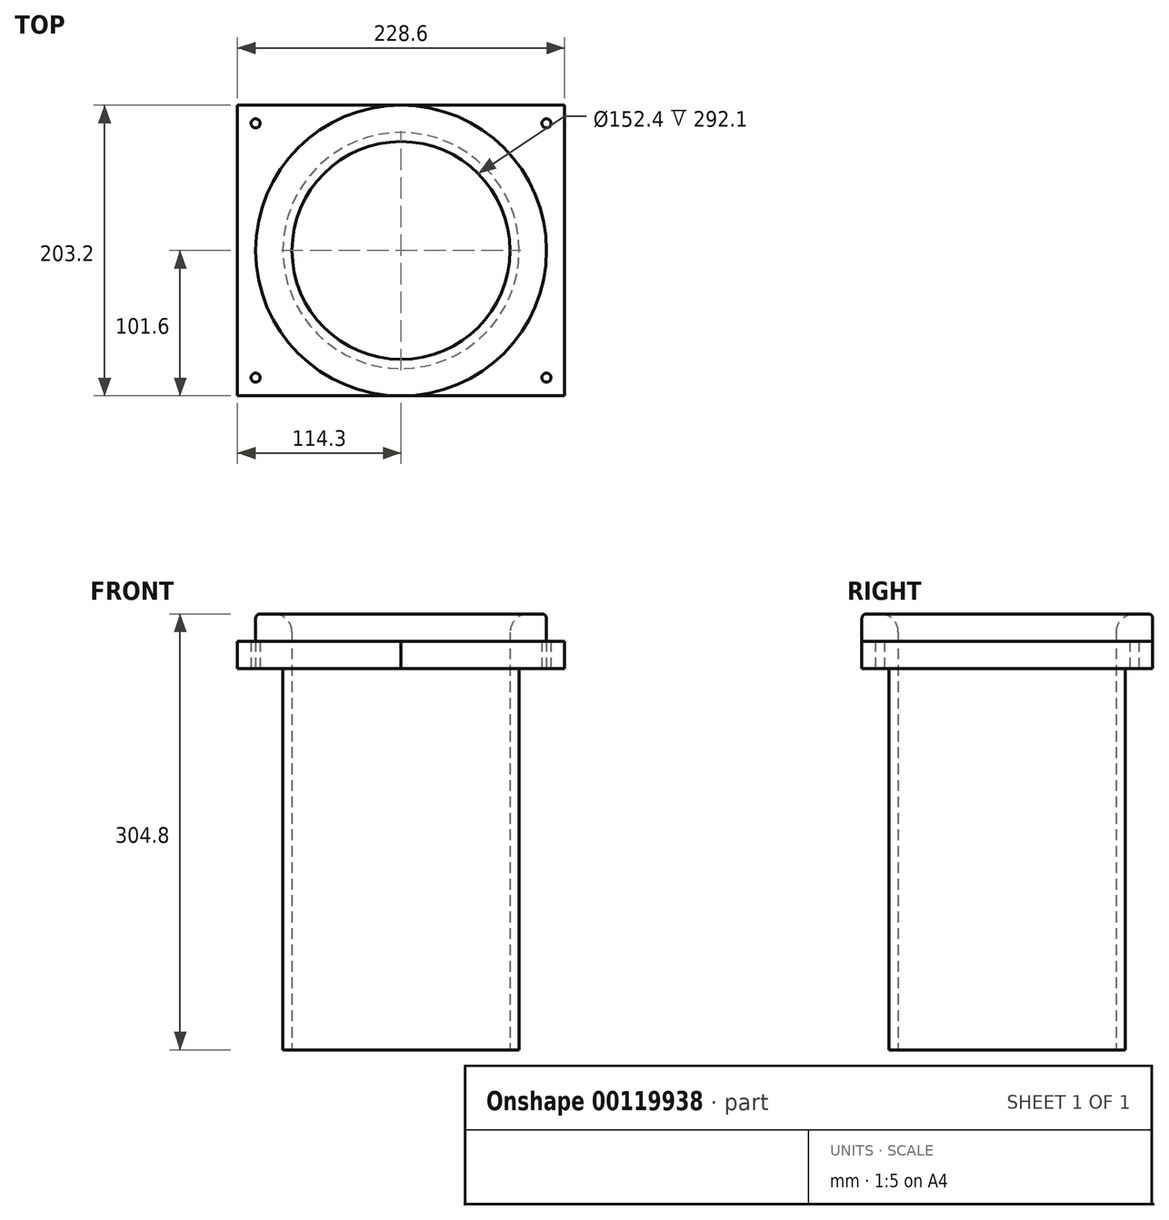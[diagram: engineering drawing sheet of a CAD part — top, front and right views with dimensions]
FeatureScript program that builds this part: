
annotation { "Feature Type Name" : "Feature", "Feature Type Description" : "" }
export const myFeature = defineFeature(function(context is Context, id is Id, definition is map)
    precondition{}
    {
        {
            var Q0;
            Q0=qCreatedBy(makeId("Top.planeOp"),FACE);
            var sketch = newSketch(context, id + "F0", { "sketchPlane" : qUnion([Q0])});
            skLineSegment(sketch, "E0.bottom", {"start": v(0, 0) * mm, "end": v(228.6, 0) * mm});
            skLineSegment(sketch, "E0.top", {"start": v(0, 203.2) * mm, "end": v(228.6, 203.2) * mm});
            skLineSegment(sketch, "E0.left", {"start": v(0, 0) * mm, "end": v(0, 203.2) * mm});
            skLineSegment(sketch, "E0.right", {"start": v(228.6, 0) * mm, "end": v(228.6, 203.2) * mm});
            skCircle(sketch, "E1", {"center": v(114.3, 101.6) * mm, "radius": 76.2 * mm});
            skCircle(sketch, "E2", {"center": v(114.3, 101.6) * mm, "radius": 82.55 * mm});
            skCircle(sketch, "E3", {"center": v(114.3, 101.6) * mm, "radius": 101.6 * mm});
            skCircle(sketch, "E4", {"center": v(12.7, 190.5) * mm, "radius": 3.18 * mm});
            skCircle(sketch, "E5", {"center": v(12.7, 12.7) * mm, "radius": 3.18 * mm});
            skCircle(sketch, "E6", {"center": v(215.9, 12.7) * mm, "radius": 3.18 * mm});
            skCircle(sketch, "E7", {"center": v(215.9, 190.5) * mm, "radius": 3.18 * mm});
            skSolve(sketch);
        }
        {
            var Q0;
            {var subQ5=sQuery(id+"F0.wireOp",EDGE,"E0.left");Q0=makeQuery(id+"F0.imprint","IMPRINT",FACE,{"disambiguationData":[TD([[makeQuery(id+"F0.imprint","IMPRINT",EDGE,{"derivedFrom":subQ5}),-1.0]])]});}
            var Q1;
            {var subQ5=sQuery(id+"F0.wireOp",EDGE,"E0.right");Q1=makeQuery(id+"F0.imprint","IMPRINT",FACE,{"disambiguationData":[TD([[makeQuery(id+"F0.imprint","IMPRINT",EDGE,{"derivedFrom":subQ5}),1.0]])]});}
            extrude(context, id + "F1", {"entities" : qUnion([Q0, Q1]), "depth" : 19.05 * mm});
        }
        {
            var Q0;
            Q0=makeQuery(id+"F0.imprint","IMPRINT",FACE,{"disambiguationData":[TD([[makeQuery(id+"F0.imprint","IMPRINT",EDGE,{"derivedFrom":sQuery(id+"F0.wireOp",EDGE,"E2")}),-1.0]])]});
            var Q1;
            Q1=makeQuery(id+"F0.imprint","IMPRINT",FACE,{"disambiguationData":[TD([[makeQuery(id+"F0.imprint","IMPRINT",EDGE,{"derivedFrom":sQuery(id+"F0.wireOp",EDGE,"E1")}),-1.0]])]});
            extrude(context, id + "F2", {"entities" : qUnion([Q0, Q1]), "depth" : 38.1 * mm});
        }
        {
            var Q0;
            Q0=makeQuery(id+"F0.imprint","IMPRINT",FACE,{"disambiguationData":[TD([[makeQuery(id+"F0.imprint","IMPRINT",EDGE,{"derivedFrom":sQuery(id+"F0.wireOp",EDGE,"E1")}),-1.0]])]});
            extrude(context, id + "F3", {"entities" : qUnion([Q0]), "operationType" : NewBodyOperationType.ADD, "oppositeDirection" : true, "depth" : 266.7 * mm});
        }
        {
            var Q0;
            Q0=makeQuery(id+"F2.opExtrude","CAP_EDGE",EDGE,{"disambiguationData":[OSD([sQuery(id+"F0.wireOp",EDGE,"E1")])],"isStart":false});
            fillet(context, id + "F4", {"entities" : qUnion([Q0]), "radius" : 12.7 * mm, "tangentPropagation" : true, "allowEdgeOverflow" : false});
        }
        {
            var Q0;
            Q0=makeQuery(id+"F2.opExtrude","CAP_EDGE",EDGE,{"disambiguationData":[OSD([sQuery(id+"F0.wireOp",EDGE,"E3")])],"isStart":false});
            fillet(context, id + "F5", {"entities" : qUnion([Q0]), "radius" : 3.17 * mm, "tangentPropagation" : true, "allowEdgeOverflow" : false});
        }
    });
